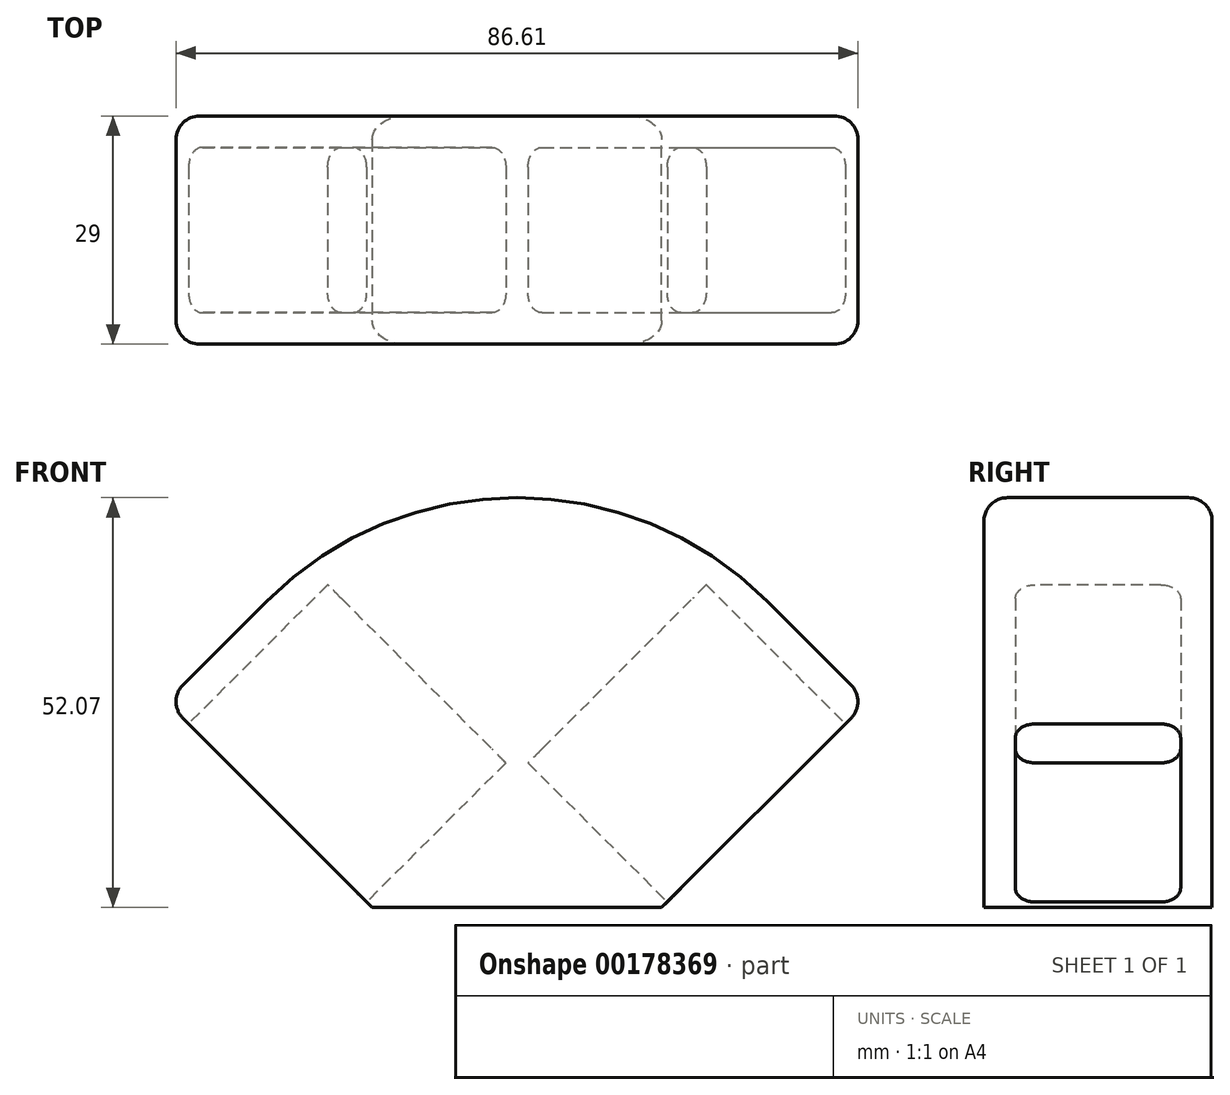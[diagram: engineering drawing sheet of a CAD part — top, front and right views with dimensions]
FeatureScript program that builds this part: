
annotation { "Feature Type Name" : "Feature", "Feature Type Description" : "" }
export const myFeature = defineFeature(function(context is Context, id is Id, definition is map)
    precondition{}
    {
        {
            var Q0;
            Q0=qCreatedBy(makeId("Top.planeOp"),FACE);
            var sketch = newSketch(context, id + "F0", { "sketchPlane" : qUnion([Q0])});
            skLineSegment(sketch, "E0.bottom", {"start": v(31.5, -14.5) * mm, "end": v(-31.5, -14.5) * mm});
            skLineSegment(sketch, "E0.top", {"start": v(31.5, 14.5) * mm, "end": v(-31.5, 14.5) * mm});
            skLineSegment(sketch, "E0.left", {"start": v(31.5, -14.5) * mm, "end": v(31.5, 14.5) * mm});
            skLineSegment(sketch, "E0.right", {"start": v(-31.5, -14.5) * mm, "end": v(-31.5, 14.5) * mm});
            skPoint(sketch, "E0.middle", {"position": v(0, 0) * mm});
            skLineSegment(sketch, "E1.bottom", {"start": v(4.5, -10.5) * mm, "end": v(-27.5, -10.5) * mm});
            skLineSegment(sketch, "E1.top", {"start": v(4.5, 10.5) * mm, "end": v(-27.5, 10.5) * mm});
            skLineSegment(sketch, "E1.left", {"start": v(4.5, -10.5) * mm, "end": v(4.5, 10.5) * mm});
            skLineSegment(sketch, "E1.right", {"start": v(-27.5, -10.5) * mm, "end": v(-27.5, 10.5) * mm});
            skPoint(sketch, "E1.middle", {"position": v(-11.5, 0) * mm});
            skSolve(sketch);
        }
        {
            var Q0;
            Q0=makeQuery(id+"F0.imprint","IMPRINT",FACE,{"disambiguationData":[TD([[makeQuery(id+"F0.imprint","IMPRINT",EDGE,{"derivedFrom":sQuery(id+"F0.wireOp",EDGE,"E0.bottom")}),-1.0]])]});
            var Q1;
            Q1=makeQuery(id+"F0.imprint","IMPRINT",FACE,{"disambiguationData":[TD([[makeQuery(id+"F0.imprint","IMPRINT",EDGE,{"derivedFrom":sQuery(id+"F0.wireOp",EDGE,"E1.bottom")}),-1.0]])]});
            extrude(context, id + "F1", {"entities" : qUnion([Q0, Q1]), "depth" : 63 * mm});
        }
        {
            var Q0;
            Q0=makeQuery(id+"F1.opExtrude","SWEPT_FACE",FACE,{"disambiguationData":[OSD([sQuery(id+"F0.wireOp",EDGE,"E0.left")])]});
            var sketch = newSketch(context, id + "F2", { "sketchPlane" : qUnion([Q0])});
            skLineSegment(sketch, "E2.bottom", {"start": v(10.5, 4) * mm, "end": v(-10.5, 4) * mm});
            skLineSegment(sketch, "E2.top", {"start": v(10.5, 36) * mm, "end": v(-10.5, 36) * mm});
            skLineSegment(sketch, "E2.left", {"start": v(10.5, 4) * mm, "end": v(10.5, 36) * mm});
            skLineSegment(sketch, "E2.right", {"start": v(-10.5, 4) * mm, "end": v(-10.5, 36) * mm});
            skPoint(sketch, "E2.middle", {"position": v(0, 20) * mm});
            skSolve(sketch);
        }
        {
            var Q0;
            Q0=makeQuery(id+"F2.imprint","IMPRINT",FACE,{"disambiguationData":[TD([[makeQuery(id+"F2.imprint","IMPRINT",EDGE,{"derivedFrom":sQuery(id+"F2.wireOp",EDGE,"E2.bottom")}),-1.0]])]});
            extrude(context, id + "F3", {"entities" : qUnion([Q0]), "operationType" : NewBodyOperationType.REMOVE, "oppositeDirection" : true, "depth" : 25 * mm});
        }
        {
            var Q0;
            Q0=makeQuery(id+"F1.opExtrude","CAP_EDGE",EDGE,{"disambiguationData":[OSD([sQuery(id+"F0.wireOp",EDGE,"E0.left")])],"isStart":false});
            chamfer(context, id + "F4", {"entities" : qUnion([Q0]), "width" : 26 * mm, "tangentPropagation" : true});
        }
        {
            var Q0;
            Q0=makeQuery(id+"F1.opExtrude","CAP_EDGE",EDGE,{"disambiguationData":[OSD([sQuery(id+"F0.wireOp",EDGE,"E0.right")])],"isStart":true});
            fillet(context, id + "F5", {"entities" : qUnion([Q0]), "radius" : 45 * mm, "tangentPropagation" : true, "allowEdgeOverflow" : false});
        }
        {
            var Q0;
            {var subQ0=sQuery(id+"F0.wireOp",EDGE,"E1.right");var subQ1=sQuery(id+"F0.wireOp",EDGE,"E1.left");var subQ2=sQuery(id+"F0.wireOp",EDGE,"E1.top");var subQ3=sQuery(id+"F0.wireOp",EDGE,"E1.bottom");Q0=makeQuery(id+"FpjEZIGG20a8GlO_1.boolean.opBoolean","MERGE",FACE,{"derivedFrom":[makeQuery(id+"F1.opExtrude","CAP_FACE",FACE,{"disambiguationData":[OSD([sQuery(id+"F0.wireOp",EDGE,"E0.bottom"),sQuery(id+"F0.wireOp",EDGE,"E0.top"),sQuery(id+"F0.wireOp",EDGE,"E0.left"),sQuery(id+"F0.wireOp",EDGE,"E0.right"),subQ3,subQ2,subQ1,subQ0])],"isStart":true}),makeQuery(id+"FpjEZIGG20a8GlO_1.opExtrude","CAP_FACE",FACE,{"disambiguationData":[OSD([subQ3,subQ2,subQ1,subQ0])],"isStart":true})]});}
            var Q1;
            Q1=makeQuery(id+"F1.opExtrude","SWEPT_FACE",FACE,{"disambiguationData":[OSD([sQuery(id+"F0.wireOp",EDGE,"E0.right")])]});
            var Q2;
            Q2=makeQuery(id+"F1.opExtrude","SWEPT_EDGE",EDGE,{"disambiguationData":[OSD([sQuery(id+"F0.wireOp",EDGE,"E0.bottom"),sQuery(id+"F0.wireOp",EDGE,"E0.left")])]});
            var Q3;
            Q3=makeQuery(id+"F1.opExtrude","SWEPT_EDGE",EDGE,{"disambiguationData":[OSD([sQuery(id+"F0.wireOp",EDGE,"E0.top"),sQuery(id+"F0.wireOp",EDGE,"E0.left")])]});
            var Q4;
            Q4=makeQuery(id+"F1.opExtrude","CAP_EDGE",EDGE,{"disambiguationData":[OSD([sQuery(id+"F0.wireOp",EDGE,"E0.bottom")])],"isStart":false});
            var Q5;
            Q5=makeQuery(id+"F1.opExtrude","CAP_EDGE",EDGE,{"disambiguationData":[OSD([sQuery(id+"F0.wireOp",EDGE,"E0.top")])],"isStart":false});
            fillet(context, id + "F6", {"entities" : qUnion([Q0, Q1, Q2, Q3, Q4, Q5]), "radius" : 3 * mm, "tangentPropagation" : true, "allowEdgeOverflow" : false});
        }
        {
            var Q0;
            Q0=makeQuery(id+"F1.opExtrude","CAP_FACE",FACE,{"disambiguationData":[OSD([sQuery(id+"F0.wireOp",EDGE,"E0.bottom"),sQuery(id+"F0.wireOp",EDGE,"E0.top"),sQuery(id+"F0.wireOp",EDGE,"E0.left"),sQuery(id+"F0.wireOp",EDGE,"E0.right")])],"isStart":false});
            var sketch = newSketch(context, id + "F7", { "sketchPlane" : qUnion([Q0])});
            skLineSegment(sketch, "E3.bottom", {"start": v(4.5, 10.5) * mm, "end": v(-27.5, 10.5) * mm});
            skLineSegment(sketch, "E3.top", {"start": v(4.5, -10.5) * mm, "end": v(-27.5, -10.5) * mm});
            skLineSegment(sketch, "E3.left", {"start": v(4.5, 10.5) * mm, "end": v(4.5, -10.5) * mm});
            skLineSegment(sketch, "E3.right", {"start": v(-27.5, 10.5) * mm, "end": v(-27.5, -10.5) * mm});
            skPoint(sketch, "E3.middle", {"position": v(-11.5, 0) * mm});
            skPoint(sketch, "E3.middle.positionSnap0", {"position": v(-11.5, -11.5) * mm});
            skPoint(sketch, "E3.middle.positionSnap1", {"position": v(-28.5, 0) * mm});
            skPoint(sketch, "E3.centerSnap0", {"position": v(-11.5, -11.5) * mm});
            skPoint(sketch, "E3.centerSnap1", {"position": v(-28.5, 0) * mm});
            skSolve(sketch);
        }
        {
            var Q0;
            Q0 = qSketchRegion(id + "F7", true);
            extrude(context, id + "F8", {"entities" : qUnion([Q0]), "operationType" : NewBodyOperationType.REMOVE, "oppositeDirection" : true, "depth" : 25 * mm});
        }
        {
            var Q0;
            Q0=makeQuery(id+"F3.boolean.opBoolean","COPY",EDGE,{"derivedFrom":makeQuery(id+"F3.opExtrude","SWEPT_EDGE",EDGE,{"disambiguationData":[OSD([sQuery(id+"F2.wireOp",EDGE,"E2.bottom"),sQuery(id+"F2.wireOp",EDGE,"E2.right")])]})});
            var Q1;
            Q1=makeQuery(id+"F3.boolean.opBoolean","COPY",EDGE,{"derivedFrom":makeQuery(id+"F3.opExtrude","SWEPT_EDGE",EDGE,{"disambiguationData":[OSD([sQuery(id+"F2.wireOp",EDGE,"E2.bottom"),sQuery(id+"F2.wireOp",EDGE,"E2.left")])]})});
            var Q2;
            Q2=makeQuery(id+"F3.boolean.opBoolean","COPY",EDGE,{"derivedFrom":makeQuery(id+"F3.opExtrude","SWEPT_EDGE",EDGE,{"disambiguationData":[OSD([sQuery(id+"F2.wireOp",EDGE,"E2.top"),sQuery(id+"F2.wireOp",EDGE,"E2.left")])]})});
            var Q3;
            Q3=makeQuery(id+"F3.boolean.opBoolean","COPY",EDGE,{"derivedFrom":makeQuery(id+"F3.opExtrude","SWEPT_EDGE",EDGE,{"disambiguationData":[OSD([sQuery(id+"F2.wireOp",EDGE,"E2.top"),sQuery(id+"F2.wireOp",EDGE,"E2.right")])]})});
            var Q4;
            Q4=makeQuery(id+"F8.boolean.opBoolean","COPY",EDGE,{"derivedFrom":makeQuery(id+"F8.opExtrude","SWEPT_EDGE",EDGE,{"disambiguationData":[OSD([sQuery(id+"F7.wireOp",EDGE,"E3.top"),sQuery(id+"F7.wireOp",EDGE,"E3.left")])]})});
            var Q5;
            Q5=makeQuery(id+"F8.boolean.opBoolean","COPY",EDGE,{"derivedFrom":makeQuery(id+"F8.opExtrude","SWEPT_EDGE",EDGE,{"disambiguationData":[OSD([sQuery(id+"F7.wireOp",EDGE,"E3.bottom"),sQuery(id+"F7.wireOp",EDGE,"E3.left")])]})});
            var Q6;
            Q6=makeQuery(id+"F8.boolean.opBoolean","COPY",EDGE,{"derivedFrom":makeQuery(id+"F8.opExtrude","SWEPT_EDGE",EDGE,{"disambiguationData":[OSD([sQuery(id+"F7.wireOp",EDGE,"E3.bottom"),sQuery(id+"F7.wireOp",EDGE,"E3.right")])]})});
            var Q7;
            Q7=makeQuery(id+"F8.boolean.opBoolean","COPY",EDGE,{"derivedFrom":makeQuery(id+"F8.opExtrude","SWEPT_EDGE",EDGE,{"disambiguationData":[OSD([sQuery(id+"F7.wireOp",EDGE,"E3.top"),sQuery(id+"F7.wireOp",EDGE,"E3.right")])]})});
            fillet(context, id + "F9", {"entities" : qUnion([Q0, Q1, Q2, Q3, Q4, Q5, Q6, Q7]), "radius" : 2.5 * mm, "tangentPropagation" : true, "allowEdgeOverflow" : false});
        }
        {
            var Q0;
            Q0=makeQuery(id+"F1.opExtrude","SWEPT_BODY",BODY,{"disambiguationData":[OSD([sQuery(id+"F0.wireOp",EDGE,"E0.bottom"),sQuery(id+"F0.wireOp",EDGE,"E0.top"),sQuery(id+"F0.wireOp",EDGE,"E0.left"),sQuery(id+"F0.wireOp",EDGE,"E0.right")])]});
            var Q1;
            {var subQ0=sQuery(id+"F0.wireOp",EDGE,"E0.left");Q1=makeQuery(id+"F4.opChamfer","BLEND_EDGE",EDGE,{"blendedFrom":[makeQuery(id+"F1.opExtrude","CAP_EDGE",EDGE,{"disambiguationData":[OSD([subQ0])],"isStart":false}),makeQuery(id+"F1.opExtrude","SWEPT_FACE",FACE,{"disambiguationData":[OSD([subQ0])]})],"blendedInto":[makeQuery(id+"F1.opExtrude","SWEPT_FACE",FACE,{"disambiguationData":[OSD([subQ0])]})]});}
            transform(context, id + "F10", {"entities" : qUnion([Q0]), "transformType" : TransformType.ROTATION, "transformAxis" : qUnion([Q1]), "angle" : 225 * degree, "makeCopy" : false});
        }
    });
